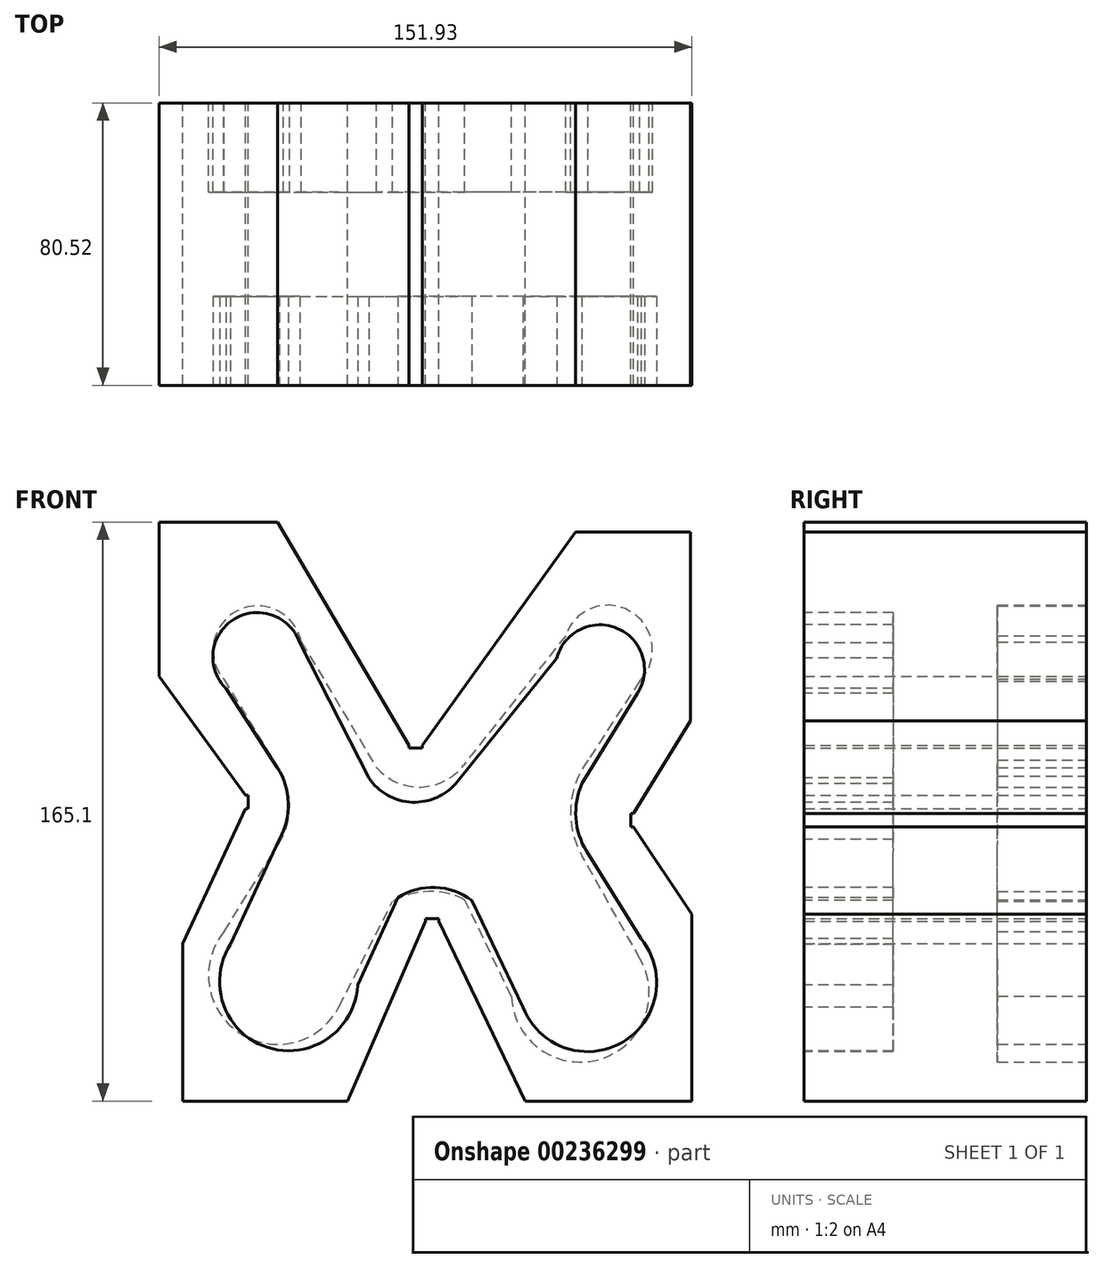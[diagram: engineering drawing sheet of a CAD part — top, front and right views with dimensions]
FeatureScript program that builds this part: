
annotation { "Feature Type Name" : "Feature", "Feature Type Description" : "" }
export const myFeature = defineFeature(function(context is Context, id is Id, definition is map)
    precondition{}
    {
        {
            var Q0;
            Q0=qCreatedBy(makeId("Front.planeOp"),FACE);
            var sketch = newSketch(context, id + "F0", { "sketchPlane" : qUnion([Q0])});
            skLineSegment(sketch, "E0", {"start": v(0, 0) * mm, "end": v(-37.45, 63.72) * mm});
            skLineSegment(sketch, "E1", {"start": v(-37.45, 63.72) * mm, "end": v(-71.24, 63.72) * mm});
            skLineSegment(sketch, "E2", {"start": v(-71.24, 63.72) * mm, "end": v(-71.24, 19.78) * mm});
            skLineSegment(sketch, "E3", {"start": v(-71.24, 19.78) * mm, "end": v(-46.6, -14.13) * mm});
            skLineSegment(sketch, "E4", {"start": v(-46.6, -14.13) * mm, "end": v(-45.85, -14.13) * mm});
            skLineSegment(sketch, "E5", {"start": v(-45.85, -14.13) * mm, "end": v(-45.85, -17.94) * mm});
            skLineSegment(sketch, "E6", {"start": v(-45.85, -17.94) * mm, "end": v(-46.6, -17.94) * mm});
            skLineSegment(sketch, "E7", {"start": v(-46.6, -17.94) * mm, "end": v(-64.46, -56.42) * mm});
            skLineSegment(sketch, "E8", {"start": v(-64.46, -56.42) * mm, "end": v(-64.46, -101.38) * mm});
            skLineSegment(sketch, "E9", {"start": v(-64.46, -101.38) * mm, "end": v(-17.47, -101.38) * mm});
            skLineSegment(sketch, "E10", {"start": v(-17.47, -101.38) * mm, "end": v(4.73, -50.1) * mm});
            skLineSegment(sketch, "E11", {"start": v(4.73, -50.1) * mm, "end": v(4.73, -49.34) * mm});
            skLineSegment(sketch, "E12", {"start": v(4.73, -49.34) * mm, "end": v(8.54, -49.34) * mm});
            skLineSegment(sketch, "E13", {"start": v(8.54, -49.34) * mm, "end": v(8.54, -50.1) * mm});
            skLineSegment(sketch, "E14", {"start": v(8.54, -50.1) * mm, "end": v(33.2, -101.38) * mm});
            skLineSegment(sketch, "E15", {"start": v(33.2, -101.38) * mm, "end": v(80.7, -101.38) * mm});
            skLineSegment(sketch, "E16", {"start": v(80.7, -101.38) * mm, "end": v(80.7, -48.04) * mm});
            skLineSegment(sketch, "E17", {"start": v(80.7, -48.04) * mm, "end": v(63.99, -23.15) * mm});
            skLineSegment(sketch, "E18", {"start": v(63.99, -23.15) * mm, "end": v(63.23, -23.15) * mm});
            skLineSegment(sketch, "E19", {"start": v(63.23, -23.15) * mm, "end": v(63.23, -19.34) * mm});
            skLineSegment(sketch, "E20", {"start": v(63.23, -19.34) * mm, "end": v(63.99, -19.34) * mm});
            skLineSegment(sketch, "E21", {"start": v(63.99, -19.34) * mm, "end": v(80.26, 7.03) * mm});
            skLineSegment(sketch, "E22", {"start": v(80.26, 7.03) * mm, "end": v(80.26, 60.88) * mm});
            skLineSegment(sketch, "E23", {"start": v(80.26, 60.88) * mm, "end": v(47.5, 60.88) * mm});
            skLineSegment(sketch, "E24", {"start": v(47.5, 60.88) * mm, "end": v(3.8, 0) * mm});
            skLineSegment(sketch, "E25", {"start": v(0, 0) * mm, "end": v(0, -0.76) * mm});
            skLineSegment(sketch, "E26", {"start": v(0, -0.76) * mm, "end": v(3.81, -0.76) * mm});
            skLineSegment(sketch, "E27", {"start": v(3.81, -0.76) * mm, "end": v(3.81, 0) * mm});
            skSolve(sketch);
        }
        {
            var Q0;
            Q0 = qSketchRegion(id + "F0", true);
            extrude(context, id + "F1", {"entities" : qUnion([Q0]), "endBound" : BoundingType.SYMMETRIC, "depth" : 80.52 * mm});
        }
        {
            var Q0;
            Q0=makeQuery(id+"F1.opExtrude","CAP_FACE",FACE,{"disambiguationData":[OSD([sQuery(id+"F0.wireOp",EDGE,"E0"),sQuery(id+"F0.wireOp",EDGE,"E1"),sQuery(id+"F0.wireOp",EDGE,"E2"),sQuery(id+"F0.wireOp",EDGE,"E3"),sQuery(id+"F0.wireOp",EDGE,"E4"),sQuery(id+"F0.wireOp",EDGE,"E5"),sQuery(id+"F0.wireOp",EDGE,"E6"),sQuery(id+"F0.wireOp",EDGE,"E7"),sQuery(id+"F0.wireOp",EDGE,"E8"),sQuery(id+"F0.wireOp",EDGE,"E9"),sQuery(id+"F0.wireOp",EDGE,"E10"),sQuery(id+"F0.wireOp",EDGE,"E11"),sQuery(id+"F0.wireOp",EDGE,"E12"),sQuery(id+"F0.wireOp",EDGE,"E13"),sQuery(id+"F0.wireOp",EDGE,"E14"),sQuery(id+"F0.wireOp",EDGE,"E15"),sQuery(id+"F0.wireOp",EDGE,"E16"),sQuery(id+"F0.wireOp",EDGE,"E17"),sQuery(id+"F0.wireOp",EDGE,"E18"),sQuery(id+"F0.wireOp",EDGE,"E19"),sQuery(id+"F0.wireOp",EDGE,"E20"),sQuery(id+"F0.wireOp",EDGE,"E21"),sQuery(id+"F0.wireOp",EDGE,"E22"),sQuery(id+"F0.wireOp",EDGE,"E23"),sQuery(id+"F0.wireOp",EDGE,"E24"),sQuery(id+"F0.wireOp",EDGE,"E25"),sQuery(id+"F0.wireOp",EDGE,"E26"),sQuery(id+"F0.wireOp",EDGE,"E27")])],"isStart":false});
            var sketch = newSketch(context, id + "F2", { "sketchPlane" : qUnion([Q0])});
            skCircle(sketch, "E28", {"center": v(-43.22, 25.21) * mm, "radius": 12.7 * mm});
            skCircle(sketch, "E29", {"center": v(54.44, 21.72) * mm, "radius": 12.7 * mm});
            skCircle(sketch, "E30", {"center": v(50.95, -67.6) * mm, "radius": 19.69 * mm});
            skCircle(sketch, "E31", {"center": v(-34.33, -67.34) * mm, "radius": 19.69 * mm});
            skLineSegment(sketch, "E32", {"start": v(-52.25, 16.28) * mm, "end": v(-37.57, -6.27) * mm});
            skLineSegment(sketch, "E33", {"start": v(-31.18, 29.23) * mm, "end": v(-11.47, -9.22) * mm});
            skLineSegment(sketch, "E34", {"start": v(42.16, 24.93) * mm, "end": v(13.82, -10.3) * mm});
            skLineSegment(sketch, "E35", {"start": v(65.33, 15.18) * mm, "end": v(49.33, -10.84) * mm});
            skLineSegment(sketch, "E36", {"start": v(-53.14, -61.53) * mm, "end": v(-37, -26.74) * mm});
            skLineSegment(sketch, "E37", {"start": v(-14.67, -68.25) * mm, "end": v(-3.13, -43.4) * mm});
            skLineSegment(sketch, "E38", {"start": v(32.57, -74.64) * mm, "end": v(17.92, -44.17) * mm});
            skLineSegment(sketch, "E39", {"start": v(68.87, -59.46) * mm, "end": v(50.68, -30.21) * mm});
            skArc(sketch, "E40", {"start": v(-37, -26.74) * mm, "mid": v(-34.4, -16.42) * mm, "end": v(-37.57, -6.27) * mm});
            skArc(sketch, "E41", {"start": v(-11.47, -9.22) * mm, "mid": v(0.9, -16.15) * mm, "end": v(13.82, -10.3) * mm});
            skArc(sketch, "E42", {"start": v(17.92, -44.17) * mm, "mid": v(7.51, -40.45) * mm, "end": v(-3.13, -43.4) * mm});
            skArc(sketch, "E43", {"start": v(49.33, -10.84) * mm, "mid": v(47.6, -20.7) * mm, "end": v(50.68, -30.21) * mm});
            skSolve(sketch);
        }
        {
            var Q0;
            Q0 = qSketchRegion(id + "F2", true);
            extrude(context, id + "F3", {"entities" : qUnion([Q0]), "operationType" : NewBodyOperationType.REMOVE, "oppositeDirection" : true, "depth" : 25.4 * mm});
        }
        {
            var Q0;
            Q0=makeQuery(id+"F1.opExtrude","CAP_FACE",FACE,{"disambiguationData":[OSD([sQuery(id+"F0.wireOp",EDGE,"E0"),sQuery(id+"F0.wireOp",EDGE,"E1"),sQuery(id+"F0.wireOp",EDGE,"E2"),sQuery(id+"F0.wireOp",EDGE,"E3"),sQuery(id+"F0.wireOp",EDGE,"E4"),sQuery(id+"F0.wireOp",EDGE,"E5"),sQuery(id+"F0.wireOp",EDGE,"E6"),sQuery(id+"F0.wireOp",EDGE,"E7"),sQuery(id+"F0.wireOp",EDGE,"E8"),sQuery(id+"F0.wireOp",EDGE,"E9"),sQuery(id+"F0.wireOp",EDGE,"E10"),sQuery(id+"F0.wireOp",EDGE,"E11"),sQuery(id+"F0.wireOp",EDGE,"E12"),sQuery(id+"F0.wireOp",EDGE,"E13"),sQuery(id+"F0.wireOp",EDGE,"E14"),sQuery(id+"F0.wireOp",EDGE,"E15"),sQuery(id+"F0.wireOp",EDGE,"E16"),sQuery(id+"F0.wireOp",EDGE,"E17"),sQuery(id+"F0.wireOp",EDGE,"E18"),sQuery(id+"F0.wireOp",EDGE,"E19"),sQuery(id+"F0.wireOp",EDGE,"E20"),sQuery(id+"F0.wireOp",EDGE,"E21"),sQuery(id+"F0.wireOp",EDGE,"E22"),sQuery(id+"F0.wireOp",EDGE,"E23"),sQuery(id+"F0.wireOp",EDGE,"E24"),sQuery(id+"F0.wireOp",EDGE,"E25"),sQuery(id+"F0.wireOp",EDGE,"E26"),sQuery(id+"F0.wireOp",EDGE,"E27")])],"isStart":true});
            var sketch = newSketch(context, id + "F4", { "sketchPlane" : qUnion([Q0])});
            skCircle(sketch, "E44", {"center": v(-56.7, 27.29) * mm, "radius": 12.7 * mm});
            skCircle(sketch, "E45", {"center": v(43.16, 27.1) * mm, "radius": 12.7 * mm});
            skCircle(sketch, "E46", {"center": v(37.47, -65.52) * mm, "radius": 19.69 * mm});
            skCircle(sketch, "E47", {"center": v(-48.82, -70.59) * mm, "radius": 19.69 * mm});
            skLineSegment(sketch, "E48", {"start": v(-65.73, 18.35) * mm, "end": v(-51.05, -4.2) * mm});
            skLineSegment(sketch, "E49", {"start": v(-44.66, 31.3) * mm, "end": v(-15.5, -5.73) * mm});
            skLineSegment(sketch, "E50", {"start": v(30.7, 29.5) * mm, "end": v(9.26, -6.26) * mm});
            skLineSegment(sketch, "E51", {"start": v(54.84, 22.1) * mm, "end": v(35.86, -8.76) * mm});
            skLineSegment(sketch, "E52", {"start": v(55.4, -57.38) * mm, "end": v(37.2, -28.13) * mm});
            skArc(sketch, "E53", {"start": v(35.86, -8.76) * mm, "mid": v(34.12, -18.62) * mm, "end": v(37.2, -28.13) * mm});
            skLineSegment(sketch, "E54", {"start": v(-29.16, -71.5) * mm, "end": v(-15.92, -43.97) * mm});
            skLineSegment(sketch, "E55", {"start": v(19.92, -74.44) * mm, "end": v(4.7, -44.46) * mm});
            skLineSegment(sketch, "E56", {"start": v(-65.97, -60.91) * mm, "end": v(-49.25, -31.29) * mm});
            skArc(sketch, "E57", {"start": v(-49.25, -31.29) * mm, "mid": v(-46.1, -17.47) * mm, "end": v(-51.05, -4.2) * mm});
            skArc(sketch, "E58", {"start": v(-15.5, -5.73) * mm, "mid": v(-3.24, -11.84) * mm, "end": v(9.26, -6.26) * mm});
            skArc(sketch, "E59", {"start": v(4.7, -44.46) * mm, "mid": v(-5.55, -41.63) * mm, "end": v(-15.92, -43.97) * mm});
            skSolve(sketch);
        }
        {
            var Q0;
            Q0 = qSketchRegion(id + "F4", true);
            extrude(context, id + "F5", {"entities" : qUnion([Q0]), "operationType" : NewBodyOperationType.REMOVE, "oppositeDirection" : true, "depth" : 25.4 * mm});
        }
    });
